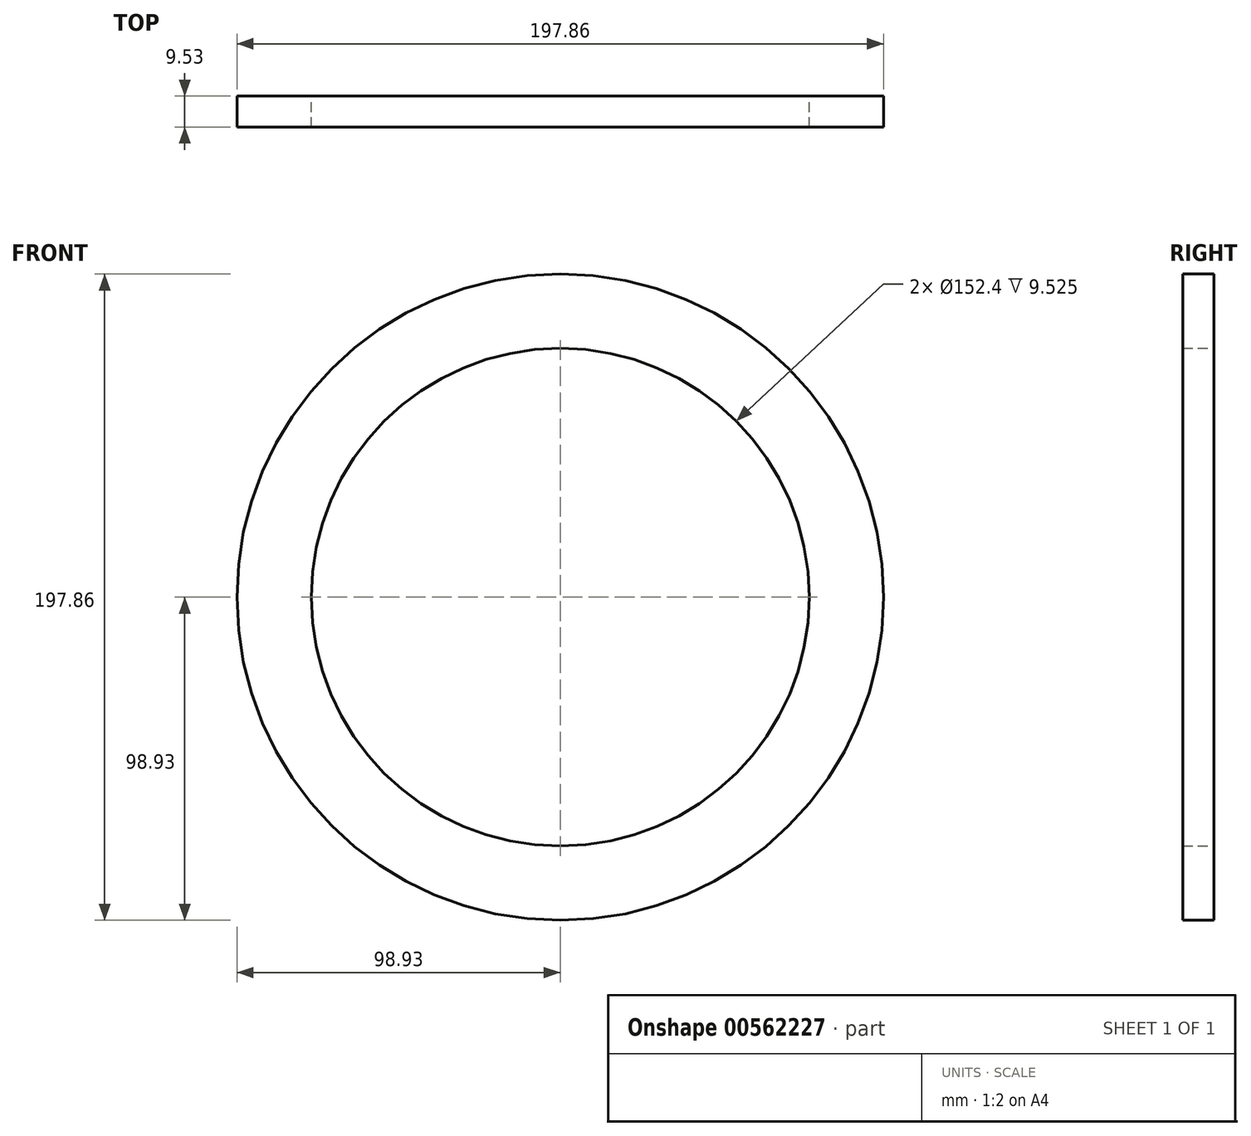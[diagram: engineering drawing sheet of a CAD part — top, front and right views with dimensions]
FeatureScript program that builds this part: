
annotation { "Feature Type Name" : "Feature", "Feature Type Description" : "" }
export const myFeature = defineFeature(function(context is Context, id is Id, definition is map)
    precondition{}
    {
        {
            var Q0;
            Q0=qCreatedBy(makeId("Front.planeOp"),FACE);
            var sketch = newSketch(context, id + "F0", { "sketchPlane" : qUnion([Q0])});
            skCircle(sketch, "E0", {"center": v(0, 0) * mm, "radius": 98.93 * mm});
            skCircle(sketch, "E1.0", {"center": v(0, 0) * mm, "radius": 76.2 * mm});
            skSolve(sketch);
        }
        {
            var Q0;
            Q0=makeQuery(id+"F0.imprint","IMPRINT",FACE,{"disambiguationData":[TD([[makeQuery(id+"F0.imprint","IMPRINT",EDGE,{"derivedFrom":sQuery(id+"F0.wireOp",EDGE,"E0")}),1.0]])]});
            extrude(context, id + "F1", {"entities" : qUnion([Q0]), "depth" : 9.52 * mm, "offsetDistance" : 25.4 * mm});
        }
    });
